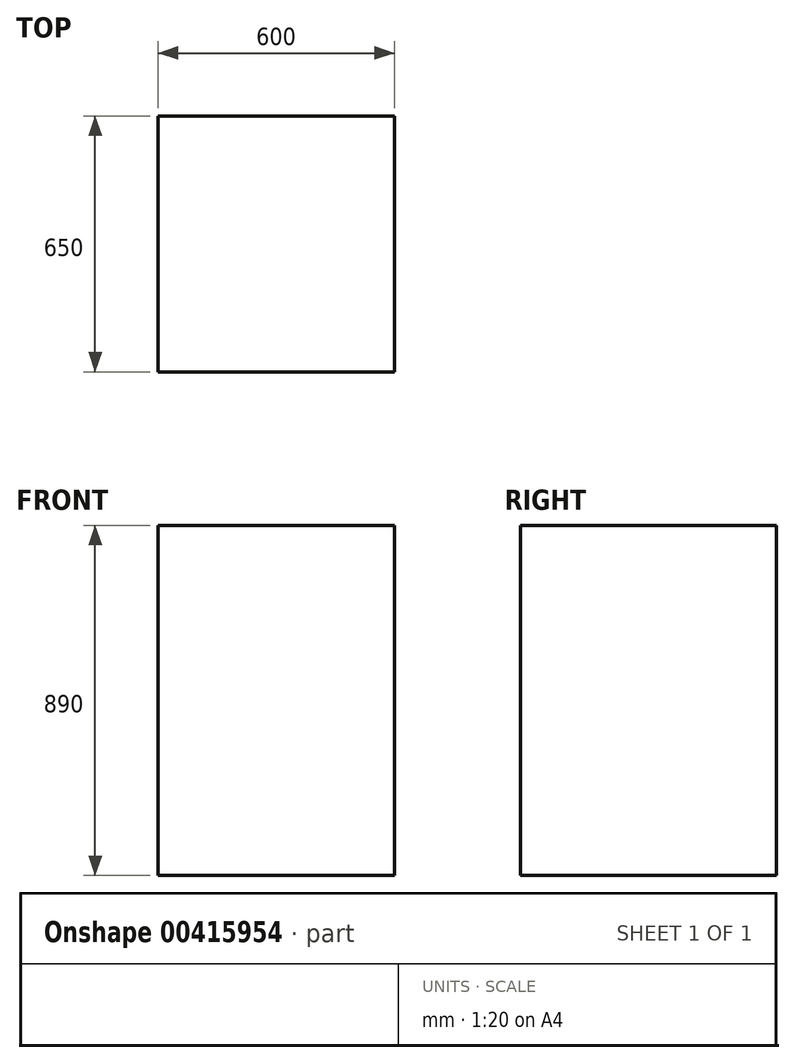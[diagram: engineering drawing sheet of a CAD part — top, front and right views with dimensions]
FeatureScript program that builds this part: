
annotation { "Feature Type Name" : "Feature", "Feature Type Description" : "" }
export const myFeature = defineFeature(function(context is Context, id is Id, definition is map)
    precondition{}
    {
        {
            var Q0;
            Q0=qCreatedBy(makeId("Top.planeOp"),FACE);
            var sketch = newSketch(context, id + "F0", { "sketchPlane" : qUnion([Q0])});
            skLineSegment(sketch, "E0.bottom", {"start": v(-1467.5, 915) * mm, "end": v(1467.5, 915) * mm});
            skLineSegment(sketch, "E0.top", {"start": v(-1467.5, -915) * mm, "end": v(1467.5, -915) * mm});
            skLineSegment(sketch, "E0.left", {"start": v(-1467.5, 915) * mm, "end": v(-1467.5, -915) * mm});
            skLineSegment(sketch, "E0.right", {"start": v(1467.5, 915) * mm, "end": v(1467.5, -915) * mm});
            skLineSegment(sketch, "E1", {"start": v(-1467.5, -915) * mm, "end": v(1467.5, 915) * mm, "construction": true});
            skLineSegment(sketch, "E2.bottom", {"start": v(1417.5, 365) * mm, "end": v(1517.5, 365) * mm});
            skLineSegment(sketch, "E2.top", {"start": v(1417.5, -315) * mm, "end": v(1517.5, -315) * mm});
            skLineSegment(sketch, "E2.left", {"start": v(1417.5, 365) * mm, "end": v(1417.5, -315) * mm});
            skLineSegment(sketch, "E2.right", {"start": v(1517.5, 365) * mm, "end": v(1517.5, -315) * mm});
            skLineSegment(sketch, "E3", {"start": v(382.5, -1735) * mm, "end": v(382.5, -915) * mm});
            skArc(sketch, "E4", {"start": v(382.5, -1735) * mm, "mid": v(962.33, -1494.83) * mm, "end": v(1202.5, -915) * mm});
            skSolve(sketch);
        }
        {
            var Q0;
            Q0=qCreatedBy(makeId("Top.planeOp"),FACE);
            var sketch = newSketch(context, id + "F1", { "sketchPlane" : qUnion([Q0])});
            skLineSegment(sketch, "E5.bottom", {"start": v(-867.5, 915) * mm, "end": v(-1467.5, 915) * mm});
            skLineSegment(sketch, "E5.top", {"start": v(-867.5, 265) * mm, "end": v(-1467.5, 265) * mm});
            skLineSegment(sketch, "E5.left", {"start": v(-867.5, 915) * mm, "end": v(-867.5, 265) * mm});
            skLineSegment(sketch, "E5.right", {"start": v(-1467.5, 915) * mm, "end": v(-1467.5, 265) * mm});
            skSolve(sketch);
        }
        {
            var Q0;
            Q0=makeQuery(id+"F1.imprint","IMPRINT",FACE,{"disambiguationData":[TD([[makeQuery(id+"F1.imprint","IMPRINT",EDGE,{"derivedFrom":sQuery(id+"F1.wireOp",EDGE,"E5.bottom")}),1.0]])]});
            extrude(context, id + "F2", {"entities" : qUnion([Q0]), "depth" : 890 * mm});
        }
        {
            var Q0;
            {var subQ7=sQuery(id+"F0.wireOp",EDGE,"E0.bottom");Q0=makeQuery(id+"F0.imprint","IMPRINT",FACE,{"disambiguationData":[TD([[makeQuery(id+"F0.imprint","IMPRINT",EDGE,{"derivedFrom":subQ7}),-1.0]])]});}
            var Q1;
            Q1=sQuery(id+"F0.wireOp",EDGE,"E0.bottom");
            var Q2;
            Q2=sQuery(id+"F0.wireOp",EDGE,"E0.right");
            var Q3;
            Q3=sQuery(id+"F0.wireOp",EDGE,"E0.left");
            extrude(context, id + "F3", {"entities" : qUnion([Q0]), "bodyType" : ToolBodyType.SURFACE, "surfaceEntities" : qUnion([Q1, Q2, Q3]), "depth" : 2570 * mm});
        }
        {
            var Q0;
            Q0=makeQuery(id+"F3.opExtrude","SWEPT_FACE",FACE,{"disambiguationData":[OSD([sQuery(id+"F0.wireOp",EDGE,"E0.right")])]});
            var sketch = newSketch(context, id + "F4", { "sketchPlane" : qUnion([Q0])});
            skLineSegment(sketch, "E6.bottom", {"start": v(315, 1930) * mm, "end": v(-365, 1930) * mm});
            skLineSegment(sketch, "E6.top", {"start": v(315, 960) * mm, "end": v(-365, 960) * mm});
            skLineSegment(sketch, "E6.left", {"start": v(315, 1930) * mm, "end": v(315, 960) * mm});
            skLineSegment(sketch, "E6.right", {"start": v(-365, 1930) * mm, "end": v(-365, 960) * mm});
            skSolve(sketch);
        }
        {
            var Q0;
            Q0=makeQuery(id+"F4.imprint","IMPRINT",FACE,{"disambiguationData":[TD([[makeQuery(id+"F4.imprint","IMPRINT",EDGE,{"derivedFrom":sQuery(id+"F4.wireOp",EDGE,"E6.bottom")}),1.0]])]});
            var Q1;
            Q1=sQuery(id+"F4.wireOp",EDGE,"E6.right");
            var Q2;
            Q2=sQuery(id+"F4.wireOp",EDGE,"E6.bottom");
            var Q3;
            Q3=sQuery(id+"F4.wireOp",EDGE,"E6.left");
            var Q4;
            Q4=sQuery(id+"F4.wireOp",EDGE,"E6.top");
            extrude(context, id + "F5", {"entities" : qUnion([Q0]), "operationType" : NewBodyOperationType.REMOVE, "surfaceEntities" : qUnion([Q1, Q2, Q3, Q4]), "endBound" : BoundingType.UP_TO_NEXT, "depth" : 630 * mm});
        }
    });
